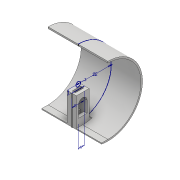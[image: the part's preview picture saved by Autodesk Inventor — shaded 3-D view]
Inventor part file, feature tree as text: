
AUTODESK INVENTOR PART (.ipt)
format: ipt  version: 2017 (Build 210142000, 142)  size: 160,256 bytes
history: native  units: mm
features: sketch x5, extrude x5, projected_geometry x2, chamfer x1, fillet x1
ambient origin geometry x8: Origin, YZ Plane, XZ Plane, XY Plane, X Axis, Y Axis, Z Axis, Center Point
bodies: Solid1 (feature_tree)
feature tree (14):
  sketch  "Sketch1"  dims[d0=22.0mm d1=3.0mm]
  extrude  "Extrusion1"  Depth=22.0mm
  extrude  "Extrusion2"  Depth=8.0mm
  extrude  "Extrusion3"  Depth=21.0mm
  extrude  "Extrusion4"  Depth=38.0mm TaperAngle=0.0deg
  extrude  "Extrusion5"  Depth=2.0mm
  chamfer  "Chamfer1"  Distance=38.0mm
  fillet  "Fillet1"  [1 undecoded]
  sketch  "Sketch2"  dims[d2=4.0mm d3=8.0mm]
  sketch  "Sketch3"  dims[d4=21.0mm d5=3.0mm]
  projected_geometry  "Projected Loop1"
  sketch  "Sketch4"  dims[d6=6.0mm d7=0.0mm d8=38.0mm d9=0.0mm]
  sketch  "Sketch5"  dims[d10=5.5mm d11=2.0mm d12=38.0mm d13=0.0mm d14=0.0mm d15=0.0mm d16=10.0mm d17=3.0mm d18=38.0mm d19=0.0mm d20=2.0mm d21=2.0mm d22=45.0deg d23=2.75mm]
  projected_geometry  "Projected Loop2"
note: 1 required parameter value undecoded (feature->parameter linkage not recoverable at this tier; creation-order binding heuristic only, values carry confidence <= 0.55)
